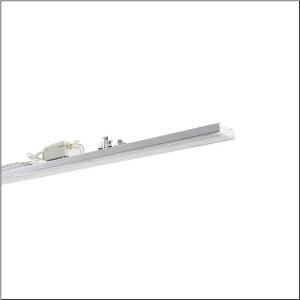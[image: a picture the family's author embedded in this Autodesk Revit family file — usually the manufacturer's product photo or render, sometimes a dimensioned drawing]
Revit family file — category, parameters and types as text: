
# Revit family: licross_r__21_recessed_ho_52tl11dv4l2s_4f4e
name_source: partatom
category: Lighting Fixtures
units: mm (PartAtom-declared; Revit-internal decimal feet)

## family parameters
Cut with Voids When Loaded = No
Host = Face
Light Source = No
Part Type = Normal
Room Calculation Point = No
Round Connector Dimension = Use Diameter
Shared = No

## types (1)
- --- (1 x LED, 22660 lm, 125.6 W, 4000K)
    Apparent Load = 126 VA
    CIE Flux Codes = 87 95 99 100 100
    Color Rendering = 80
    Color Temperature = 4000K
    Default Elevation = 1800 mm
    Description = Licross® 21 Recessed HO, luminaire insert, of sheet steel, galvanised, coil coated, white, length: 2.250mm, width: 66mm, height: 67mm, LED rated luminous flux: 22.660lm, light colour: 840, control gear: DALI 2, with plug, 5-pole, with phase selection, mains connection: 220..240V, AC, 50/60Hz, rated input power: 126W, halogen-free wiring, primary light control with lens, of plastic, primary optical cover: cover, of PMMA, light emission: direct distribution, primary light characteristic: symmetric, protection rating (complete): IP40, insulation class (complete): insulation class I (protective earthing), certification: CE, ENEC, VDE, UKCA, protection symbol: D if used in an environment without relevant dust loads with corresponding accessories, impact resistance: IK06, permissible ambient temperature for indoor applications: -40..+30°C, corresponds to IFS (International Featured Standards) requirements for safety and quality in the food industry, reducing of maximum allowable ambient temperature of 5°C with ceiling mounting, LABS conformity tested according to VDMA 24364:2018-05, packaging unit: 1 piece
    Height = 58 mm
    Lamp = 1 x LED
    Lamp Light Flux = 22660 lm
    Lamp Power = 125.6 W
    Lamp count = 1
    Length = 2250 mm
    Luminous efficacy = 180 lm/W
    Manufacturer = Siteco
    ModVariant = No
    Model = 52TL11DV4L2S
    Mounting Place = Ceiling
    Mounting Type = Pendant
    Number of Poles = 1
    OnlyDefault = Yes
    Power Factor = 1
    Product Name = Licross® 21 Recessed HO
    Product group = luminaire insert
    ProductGroupID = 901
    Protection Class = Protection class I
    Protection Degree = IP 40
    RLX_Detail_Level = 1
    RLX_Emergency_Light_Flux = 0 lm
    RLX_Emergency_Type = 0
    RLX_Emergency_Type_DB = No
    RlxData = <blob elided: 29529 chars, md5=f16236ea>
    Socket = socket
    Standby Power = 0 W
    System Light Flux = 22659 lm
    System Power = 126 W
    Type Comments = factory setting: luminous flux: 100 % | dim-lin: 254 | 489 mA
    Type Image = l_1296930.jpg
    URL = http://relux.com
    VarID = @adj_059031
    Voltage = 0 V
    Weight = 0.00 kg
    Width = 66 mm

## geometry (parser evidence)
native form markers: Blend x4, Sweep x9
no freeform markers — native parametric forms only
